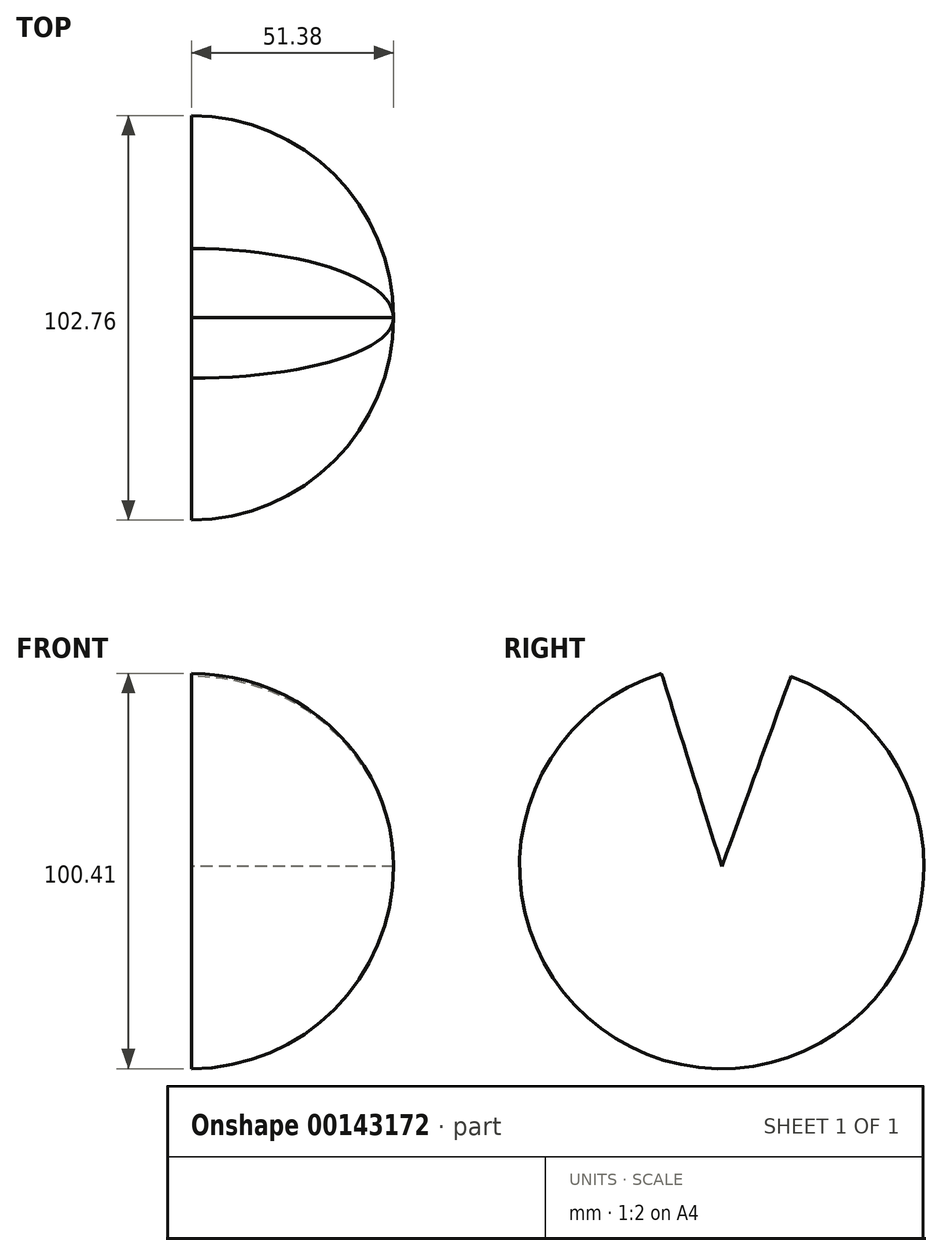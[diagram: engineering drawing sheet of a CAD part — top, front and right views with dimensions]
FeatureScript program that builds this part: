
annotation { "Feature Type Name" : "Feature", "Feature Type Description" : "" }
export const myFeature = defineFeature(function(context is Context, id is Id, definition is map)
    precondition{}
    {
        {
            var Q0;
            Q0=qCreatedBy(makeId("Front.planeOp"),FACE);
            var sketch = newSketch(context, id + "F0", { "sketchPlane" : qUnion([Q0])});
            skArc(sketch, "E0", {"start": v(51.38, 0) * mm, "mid": v(36.33, 36.33) * mm, "end": v(0, 51.38) * mm});
            skLineSegment(sketch, "E1", {"start": v(0, 51.38) * mm, "end": v(0, 0) * mm});
            skLineSegment(sketch, "E2", {"start": v(51.38, 0) * mm, "end": v(0, 0) * mm});
            skSolve(sketch);
        }
        {
            var Q0;
            Q0=makeQuery(id+"F0.imprint","IMPRINT",FACE,{"disambiguationData":[TD([[makeQuery(id+"F0.imprint","IMPRINT",EDGE,{"derivedFrom":sQuery(id+"F0.wireOp",EDGE,"E0")}),1.0]])]});
            var Q1;
            Q1=sQuery(id+"F0.wireOp",EDGE,"E2");
            revolve(context, id + "F1", {"entities" : qUnion([Q0]), "axis" : qUnion([Q1]), "revolveType" : RevolveType.FULL});
        }
        {
            var Q0;
            Q0=makeQuery(id+"F1.opRevolve","SWEPT_FACE",FACE,{"disambiguationData":[OSD([sQuery(id+"F0.wireOp",EDGE,"E1")])]});
            var sketch = newSketch(context, id + "F2", { "sketchPlane" : qUnion([Q0])});
            skLineSegment(sketch, "E3", {"start": v(0, 0) * mm, "end": v(-17.55, 48.29) * mm});
            skLineSegment(sketch, "E4", {"start": v(0, 0) * mm, "end": v(15.35, 49.03) * mm});
            skArc(sketch, "E5", {"start": v(15.35, 49.03) * mm, "mid": v(-1.16, 51.37) * mm, "end": v(-17.55, 48.29) * mm});
            skSolve(sketch);
        }
        {
            var Q0;
            Q0 = qSketchRegion(id + "F2", true);
            extrude(context, id + "F3", {"entities" : qUnion([Q0]), "operationType" : NewBodyOperationType.REMOVE, "oppositeDirection" : true, "depth" : 63.5 * mm});
        }
    });
